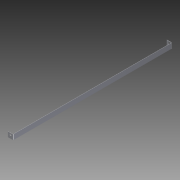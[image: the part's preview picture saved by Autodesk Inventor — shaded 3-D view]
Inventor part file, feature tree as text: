
AUTODESK INVENTOR PART (.ipt)
format: ipt  version: 2014 SP1 (Build 180222100, 222)  size: 122,880 bytes
history: native  units: in
note: dims shown in document units (in); Inventor stores cm internally (conversion verified against a paired STEP export)
features: sketch x4, extrude x3, sheet_metal_op x3, mirror x1, other x1
ambient origin geometry x8: Origin, YZ Plane, XZ Plane, XY Plane, X Axis, Y Axis, Z Axis, Center Point
bodies: Solid1 (feature_tree)
feature tree (12):
  extrude  "Extrusion1"  Depth=0.75in
  extrude  "Extrusion2"  Depth=0.0312in TaperAngle=0.0deg
  sheet_metal_op  "Flange1"
  extrude  "Extrusion3"  Depth=0.0312in
  mirror  "Mirror1"
  sketch  "Sketch1"  dims[d0=0.75in d1=0.75in]
  sketch  "Sketch2"  dims[d2=0.0312in d3=11.75in d4=0.0in]
  sketch  "Sketch3"  dims[d5=0.125in d6=0.0in d7=0.0312in]
  other  "Plate1"
  sheet_metal_op  "Bend1"
  sheet_metal_op  "Corner1"
  sketch  "Sketch4"  dims[d8=0.0156in d9=0.0625in d10=0.0312in d11=0.75in d12=90.0deg d13=0.025in d14=0.125in d15=0.0312in d16=0.0312in d17=0.5in d18=0.266in d19=0.125in d20=0.0in]
